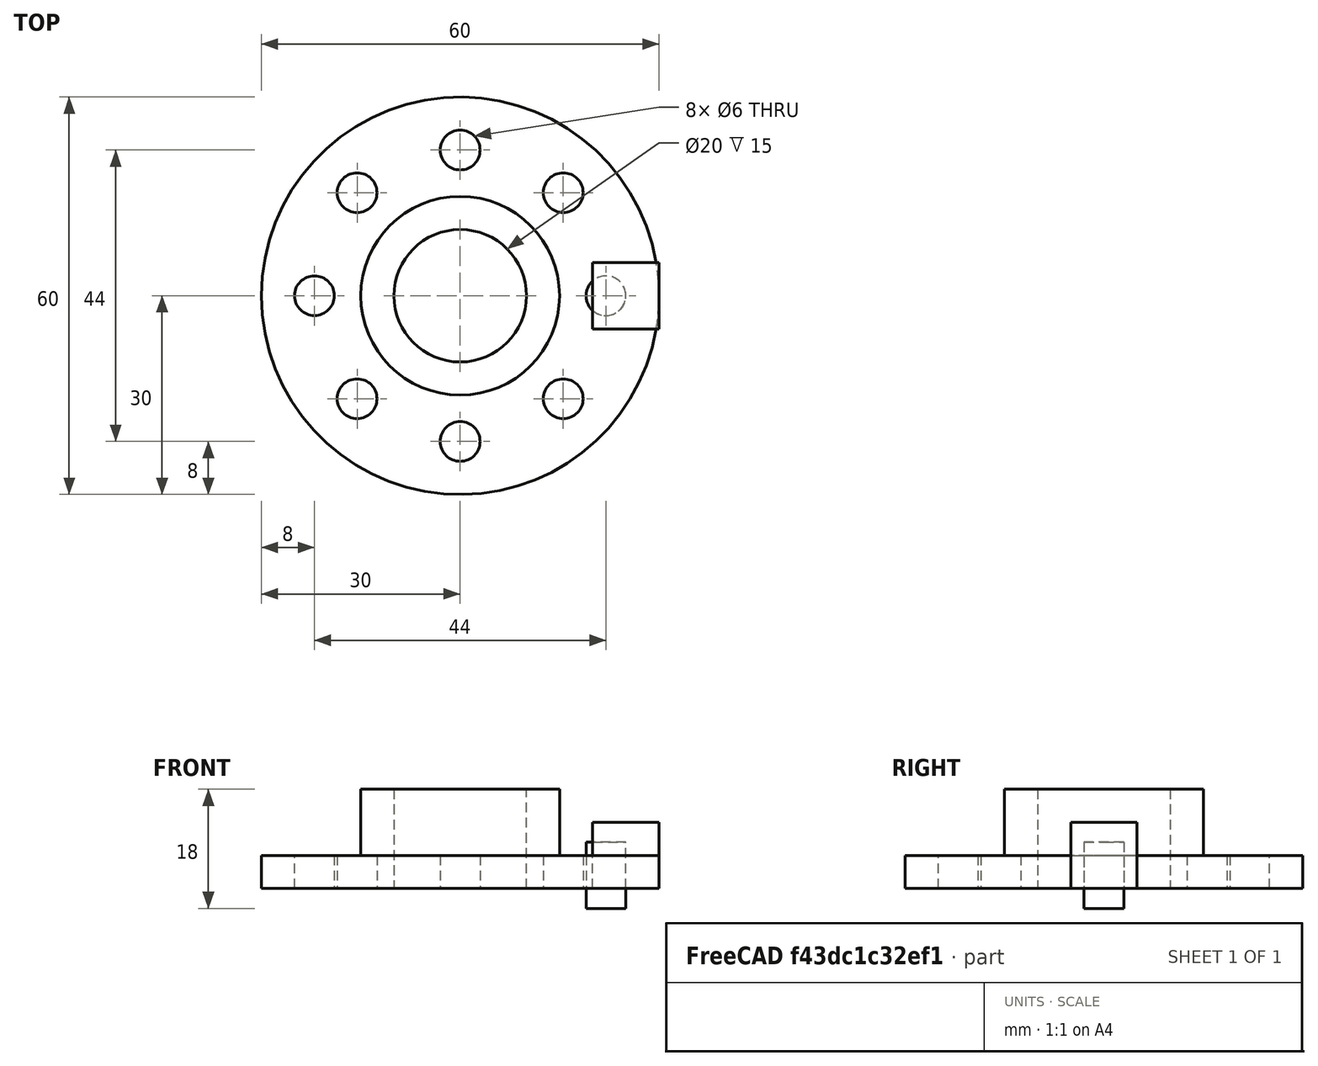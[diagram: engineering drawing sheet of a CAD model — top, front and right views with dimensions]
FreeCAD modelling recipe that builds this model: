
FCSTD DOCUMENT  (FreeCAD 1.0R39319 (Git))
Label: ojt1_t11p01_brida
License: All rights reserved
LicenseURL: https://en.wikipedia.org/wiki/All_rights_reserved
objects: Part::Cylinder×4, Part::FeaturePython×2, Part::Cut×2, Part::Box×1, Part::MultiFuse×1
note: 8 computed .brp shape members not serialized (recipe doc carries the construction recipe); baked Part::Feature solids carry a one-line shape summary decoded from their .brp

FEATURE [Part::Box] Box  label="Cub"
  AttacherType = Attacher::AttachEngine3D
  Height = 10
  Length = 10
  Placement = pos=(20,-5,0) rot=(0,0,1;0rad)
  Width = 10
FEATURE [Part::FeaturePython] Array  # Draft array (typed FeaturePython)
  AlwaysSyncPlacement = false
  Angle = 180
  ArrayType = 1
  Axis = (0,0,1)
  Base = -> Box
  Center = (0,0,0)
  Count = 6
  ExpandArray = false
  Fuse = false
  IntervalAxis = (0,0,0)
  IntervalX = (50,0,0)
  IntervalY = (0,50,0)
  IntervalZ = (0,0,50)
  NumberCircles = 3
  NumberPolar = 6
  NumberX = 2
  NumberY = 2
  NumberZ = 1
  PlacementList = 6 placements: [(20,-5,0),(19.1193,7.71062,0),(10.9356,17.476,0),(-1.42506,20.5662,0),(-13.2414,15.8008,0),(-20,5,0)]
  RadialDistance = 50
  ScaleList = (6) [(1,1,1),(1,1,1),(1,1,1),(1,1,1),(1,1,1),(1,1,1)]
  Symmetry = 1
  TangentialDistance = 25
FEATURE [Part::Cylinder] Cylinder  label="Cilindre"
  Angle = 360
  AttacherType = Attacher::AttachEngine3D
  FirstAngle = 0
  Height = 5
  Radius = 30
  SecondAngle = 0
FEATURE [Part::Cylinder] Cylinder001  label="Cilindre001"
  Angle = 360
  AttacherType = Attacher::AttachEngine3D
  FirstAngle = 0
  Height = 15
  Radius = 15
  SecondAngle = 0
FEATURE [Part::Cylinder] Cylinder002  label="Cilindre002"
  Angle = 360
  AttacherType = Attacher::AttachEngine3D
  FirstAngle = 0
  Height = 30
  Placement = pos=(0,0,-4) rot=(0,0,1;0rad)
  Radius = 10
  SecondAngle = 0
FEATURE [Part::MultiFuse] Fusion
  Refine = true
  Shapes = -> [Cylinder,Cylinder001]
FEATURE [Part::Cut] Cut
  Base = -> Fusion
  Refine = true
  Tool = -> Cylinder002
FEATURE [Part::Cylinder] Cylinder003  label="Cilindre003"
  Angle = 360
  AttacherType = Attacher::AttachEngine3D
  FirstAngle = 0
  Height = 10
  Placement = pos=(22,0,-3) rot=(0,0,1;0rad)
  Radius = 3
  SecondAngle = 0
FEATURE [Part::FeaturePython] Array001  # Draft array (typed FeaturePython)
  AlwaysSyncPlacement = false
  Angle = 360
  ArrayType = 1
  Axis = (0,0,1)
  Base = -> Cylinder003
  Center = (0,0,0)
  Count = 8
  ExpandArray = false
  Fuse = false
  IntervalAxis = (0,0,0)
  IntervalX = (50,0,0)
  IntervalY = (0,50,0)
  IntervalZ = (0,0,50)
  NumberCircles = 3
  NumberPolar = 8
  NumberX = 2
  NumberY = 2
  NumberZ = 1
  PlacementList = 8 placements: [(22,0,-3),(15.5563,15.5563,-3),(0,22,-3),(-15.5563,15.5563,-3),(-22,2.69422e-15,-3),(-15.5563,-15.5563,-3),(-4.88498e-15,-22,-3),(15.5563,-15.5563,-3)]
  RadialDistance = 50
  ScaleList = (8) [(1,1,1),(1,1,1),(1,1,1),(1,1,1),(1,1,1),(1,1,1),(1,1,1),(1,1,1)]
  Symmetry = 1
  TangentialDistance = 25
FEATURE [Part::Cut] Cut001
  Base = -> Cut
  Refine = true
  Tool = -> Array001
